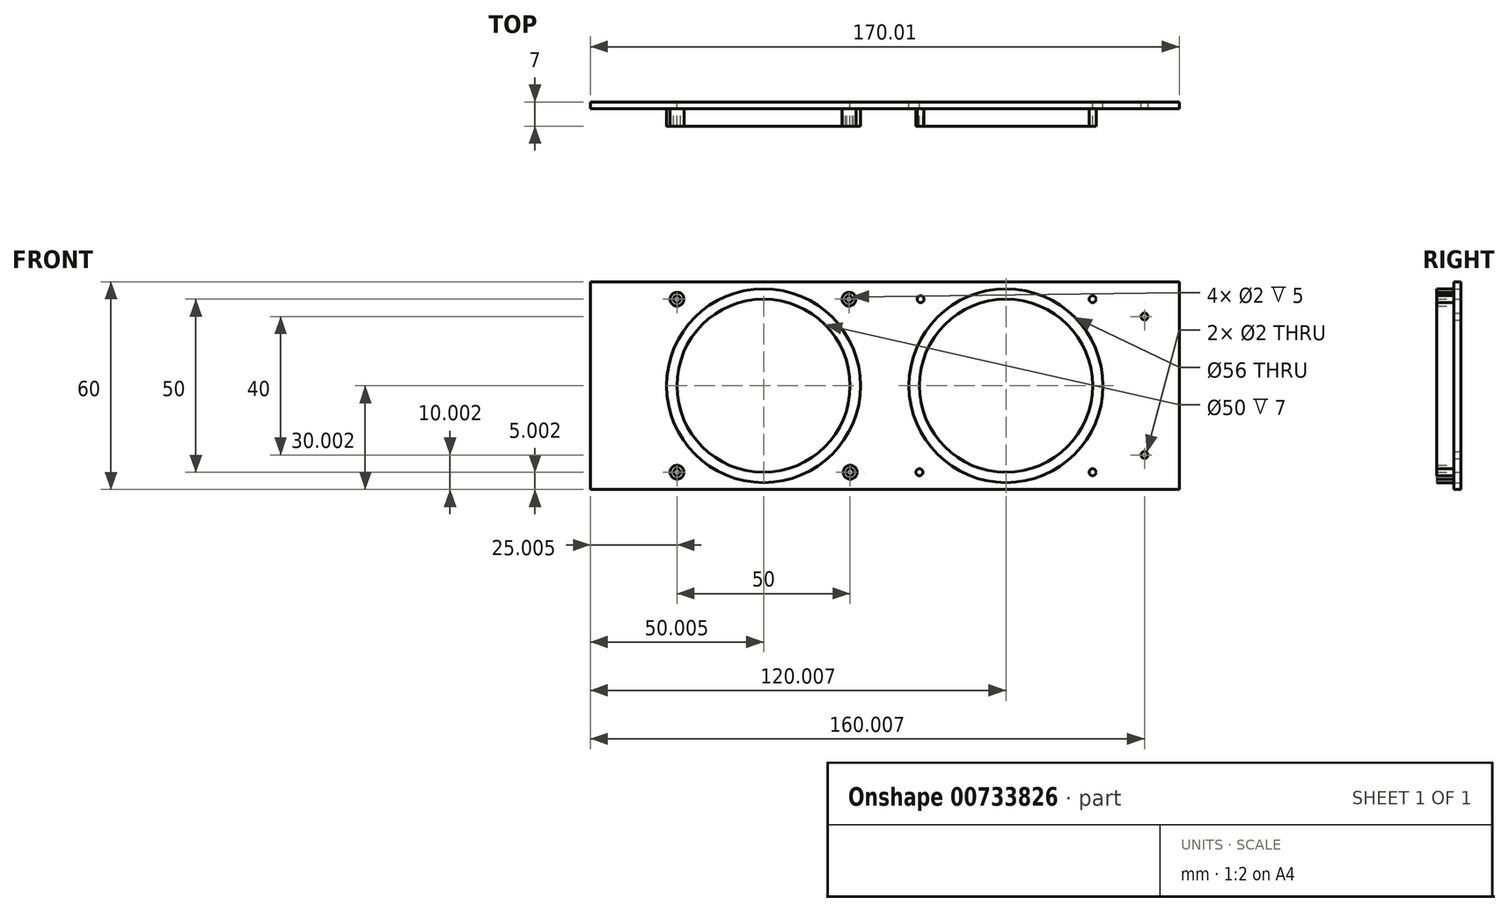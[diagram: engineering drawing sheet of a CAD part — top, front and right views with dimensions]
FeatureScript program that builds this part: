
annotation { "Feature Type Name" : "Feature", "Feature Type Description" : "" }
export const myFeature = defineFeature(function(context is Context, id is Id, definition is map)
    precondition{}
    {
        {
            var Q0;
            Q0=qCreatedBy(makeId("Front.planeOp"),FACE);
            var sketch = newSketch(context, id + "F0", { "sketchPlane" : qUnion([Q0])});
            skLineSegment(sketch, "E0.1", {"start": v(-21.17, -79.97) * mm, "end": v(-21.17, -19.97) * mm});
            skCircle(sketch, "E1", {"center": v(-11.17, -69.97) * mm, "radius": 1 * mm});
            skCircle(sketch, "E2", {"center": v(-11.17, -29.97) * mm, "radius": 1 * mm});
            skCircle(sketch, "E3", {"center": v(28.83, -49.97) * mm, "radius": 25 * mm});
            skCircle(sketch, "E4", {"center": v(53.5, -24.97) * mm, "radius": 1 * mm});
            skCircle(sketch, "E5", {"center": v(3.83, -24.97) * mm, "radius": 1 * mm});
            skCircle(sketch, "E6", {"center": v(53.83, -74.97) * mm, "radius": 1 * mm});
            skCircle(sketch, "E7", {"center": v(3.83, -74.97) * mm, "radius": 1 * mm});
            skLineSegment(sketch, "E8.MirrorCS", {"start": v(148.84, -19.97) * mm, "end": v(-21.17, -19.97) * mm});
            skLineSegment(sketch, "E9.MirrorCS", {"start": v(148.84, -79.97) * mm, "end": v(148.84, -19.97) * mm});
            skCircle(sketch, "E10.MirrorC", {"center": v(138.84, -29.97) * mm, "radius": 1 * mm});
            skCircle(sketch, "E11.MirrorC", {"center": v(138.84, -69.97) * mm, "radius": 1 * mm});
            skCircle(sketch, "E12.MirrorC", {"center": v(123.84, -74.97) * mm, "radius": 1 * mm});
            skCircle(sketch, "E13.MirrorC", {"center": v(123.84, -24.97) * mm, "radius": 1 * mm});
            skCircle(sketch, "E14.MirrorC", {"center": v(73.84, -74.97) * mm, "radius": 1 * mm});
            skCircle(sketch, "E15.MirrorC", {"center": v(74.17, -24.97) * mm, "radius": 1 * mm});
            skCircle(sketch, "E16.MirrorC", {"center": v(98.84, -49.97) * mm, "radius": 25 * mm});
            skLineSegment(sketch, "E17", {"start": v(-21.17, -79.97) * mm, "end": v(148.84, -79.97) * mm});
            skCircle(sketch, "E18", {"center": v(3.83, -24.97) * mm, "radius": 2 * mm});
            skCircle(sketch, "E19", {"center": v(3.83, -74.97) * mm, "radius": 2 * mm});
            skCircle(sketch, "E20", {"center": v(53.83, -74.97) * mm, "radius": 2 * mm});
            skCircle(sketch, "E21", {"center": v(53.5, -24.97) * mm, "radius": 2 * mm});
            skCircle(sketch, "E22", {"center": v(74.17, -24.97) * mm, "radius": 2 * mm});
            skCircle(sketch, "E23", {"center": v(73.84, -74.97) * mm, "radius": 2 * mm});
            skCircle(sketch, "E24", {"center": v(123.84, -24.97) * mm, "radius": 2 * mm});
            skCircle(sketch, "E25", {"center": v(123.84, -74.97) * mm, "radius": 2 * mm});
            skCircle(sketch, "E26", {"center": v(28.83, -49.97) * mm, "radius": 28 * mm});
            skCircle(sketch, "E27", {"center": v(98.84, -49.97) * mm, "radius": 28 * mm});
            skSolve(sketch);
        }
        {
            var Q0;
            Q0=makeQuery(id+"F0.imprint","IMPRINT",FACE,{"disambiguationData":[TD([[makeQuery(id+"F0.imprint","IMPRINT",EDGE,{"derivedFrom":sQuery(id+"F0.wireOp",EDGE,"E0.1")}),-1.0]])]});
            var Q1;
            Q1=makeQuery(id+"F0.imprint","IMPRINT",FACE,{"disambiguationData":[TD([[makeQuery(id+"F0.imprint","IMPRINT",EDGE,{"derivedFrom":sQuery(id+"F0.wireOp",EDGE,"E3")}),-1.0]])]});
            var Q2;
            Q2=makeQuery(id+"F0.imprint","IMPRINT",FACE,{"disambiguationData":[TD([[makeQuery(id+"F0.imprint","IMPRINT",EDGE,{"derivedFrom":sQuery(id+"F0.wireOp",EDGE,"E1")}),1.0]])]});
            var Q3;
            Q3=makeQuery(id+"F0.imprint","IMPRINT",FACE,{"disambiguationData":[TD([[makeQuery(id+"F0.imprint","IMPRINT",EDGE,{"derivedFrom":sQuery(id+"F0.wireOp",EDGE,"E7")}),-1.0]])]});
            var Q4;
            Q4=makeQuery(id+"F0.imprint","IMPRINT",FACE,{"disambiguationData":[TD([[makeQuery(id+"F0.imprint","IMPRINT",EDGE,{"derivedFrom":sQuery(id+"F0.wireOp",EDGE,"E7")}),1.0]])]});
            var Q5;
            Q5=makeQuery(id+"F0.imprint","IMPRINT",FACE,{"disambiguationData":[TD([[makeQuery(id+"F0.imprint","IMPRINT",EDGE,{"derivedFrom":sQuery(id+"F0.wireOp",EDGE,"E6")}),1.0]])]});
            var Q6;
            Q6=makeQuery(id+"F0.imprint","IMPRINT",FACE,{"disambiguationData":[TD([[makeQuery(id+"F0.imprint","IMPRINT",EDGE,{"derivedFrom":sQuery(id+"F0.wireOp",EDGE,"E6")}),-1.0]])]});
            var Q7;
            Q7=makeQuery(id+"F0.imprint","IMPRINT",FACE,{"disambiguationData":[TD([[makeQuery(id+"F0.imprint","IMPRINT",EDGE,{"derivedFrom":sQuery(id+"F0.wireOp",EDGE,"E14.MirrorC")}),1.0]])]});
            var Q8;
            Q8=makeQuery(id+"F0.imprint","IMPRINT",FACE,{"disambiguationData":[TD([[makeQuery(id+"F0.imprint","IMPRINT",EDGE,{"derivedFrom":sQuery(id+"F0.wireOp",EDGE,"E14.MirrorC")}),-1.0]])]});
            var Q9;
            Q9=makeQuery(id+"F0.imprint","IMPRINT",FACE,{"disambiguationData":[TD([[makeQuery(id+"F0.imprint","IMPRINT",EDGE,{"derivedFrom":sQuery(id+"F0.wireOp",EDGE,"E16.MirrorC")}),1.0]])]});
            var Q10;
            Q10=makeQuery(id+"F0.imprint","IMPRINT",FACE,{"disambiguationData":[TD([[makeQuery(id+"F0.imprint","IMPRINT",EDGE,{"derivedFrom":sQuery(id+"F0.wireOp",EDGE,"E12.MirrorC")}),1.0]])]});
            var Q11;
            Q11=makeQuery(id+"F0.imprint","IMPRINT",FACE,{"disambiguationData":[TD([[makeQuery(id+"F0.imprint","IMPRINT",EDGE,{"derivedFrom":sQuery(id+"F0.wireOp",EDGE,"E12.MirrorC")}),-1.0]])]});
            var Q12;
            Q12=makeQuery(id+"F0.imprint","IMPRINT",FACE,{"disambiguationData":[TD([[makeQuery(id+"F0.imprint","IMPRINT",EDGE,{"derivedFrom":sQuery(id+"F0.wireOp",EDGE,"E11.MirrorC")}),-1.0]])]});
            var Q13;
            Q13=makeQuery(id+"F0.imprint","IMPRINT",FACE,{"disambiguationData":[TD([[makeQuery(id+"F0.imprint","IMPRINT",EDGE,{"derivedFrom":sQuery(id+"F0.wireOp",EDGE,"E10.MirrorC")}),-1.0]])]});
            var Q14;
            Q14=makeQuery(id+"F0.imprint","IMPRINT",FACE,{"disambiguationData":[TD([[makeQuery(id+"F0.imprint","IMPRINT",EDGE,{"derivedFrom":sQuery(id+"F0.wireOp",EDGE,"E13.MirrorC")}),1.0]])]});
            var Q15;
            Q15=makeQuery(id+"F0.imprint","IMPRINT",FACE,{"disambiguationData":[TD([[makeQuery(id+"F0.imprint","IMPRINT",EDGE,{"derivedFrom":sQuery(id+"F0.wireOp",EDGE,"E13.MirrorC")}),-1.0]])]});
            var Q16;
            Q16=makeQuery(id+"F0.imprint","IMPRINT",FACE,{"disambiguationData":[TD([[makeQuery(id+"F0.imprint","IMPRINT",EDGE,{"derivedFrom":sQuery(id+"F0.wireOp",EDGE,"E15.MirrorC")}),1.0]])]});
            var Q17;
            Q17=makeQuery(id+"F0.imprint","IMPRINT",FACE,{"disambiguationData":[TD([[makeQuery(id+"F0.imprint","IMPRINT",EDGE,{"derivedFrom":sQuery(id+"F0.wireOp",EDGE,"E15.MirrorC")}),-1.0]])]});
            var Q18;
            Q18=makeQuery(id+"F0.imprint","IMPRINT",FACE,{"disambiguationData":[TD([[makeQuery(id+"F0.imprint","IMPRINT",EDGE,{"derivedFrom":sQuery(id+"F0.wireOp",EDGE,"E4")}),-1.0]])]});
            var Q19;
            Q19=makeQuery(id+"F0.imprint","IMPRINT",FACE,{"disambiguationData":[TD([[makeQuery(id+"F0.imprint","IMPRINT",EDGE,{"derivedFrom":sQuery(id+"F0.wireOp",EDGE,"E4")}),1.0]])]});
            var Q20;
            Q20=makeQuery(id+"F0.imprint","IMPRINT",FACE,{"disambiguationData":[TD([[makeQuery(id+"F0.imprint","IMPRINT",EDGE,{"derivedFrom":sQuery(id+"F0.wireOp",EDGE,"E5")}),-1.0]])]});
            var Q21;
            Q21=makeQuery(id+"F0.imprint","IMPRINT",FACE,{"disambiguationData":[TD([[makeQuery(id+"F0.imprint","IMPRINT",EDGE,{"derivedFrom":sQuery(id+"F0.wireOp",EDGE,"E5")}),1.0]])]});
            var Q22;
            Q22=makeQuery(id+"F0.imprint","IMPRINT",FACE,{"disambiguationData":[TD([[makeQuery(id+"F0.imprint","IMPRINT",EDGE,{"derivedFrom":sQuery(id+"F0.wireOp",EDGE,"E2")}),1.0]])]});
            extrude(context, id + "F1", {"entities" : qUnion([Q0, Q1, Q2, Q3, Q4, Q5, Q6, Q7, Q8, Q9, Q10, Q11, Q12, Q13, Q14, Q15, Q16, Q17, Q18, Q19, Q20, Q21, Q22]), "depth" : 5 * mm, "offsetDistance" : 25.4 * mm});
        }
        {
            var Q0;
            Q0=makeQuery(id+"F0.imprint","IMPRINT",FACE,{"disambiguationData":[TD([[makeQuery(id+"F0.imprint","IMPRINT",EDGE,{"derivedFrom":sQuery(id+"F0.wireOp",EDGE,"E5")}),-1.0]])]});
            var Q1;
            Q1=makeQuery(id+"F0.imprint","IMPRINT",FACE,{"disambiguationData":[TD([[makeQuery(id+"F0.imprint","IMPRINT",EDGE,{"derivedFrom":sQuery(id+"F0.wireOp",EDGE,"E4")}),-1.0]])]});
            var Q2;
            Q2=makeQuery(id+"F0.imprint","IMPRINT",FACE,{"disambiguationData":[TD([[makeQuery(id+"F0.imprint","IMPRINT",EDGE,{"derivedFrom":sQuery(id+"F0.wireOp",EDGE,"E15.MirrorC")}),1.0]])]});
            var Q3;
            Q3=makeQuery(id+"F0.imprint","IMPRINT",FACE,{"disambiguationData":[TD([[makeQuery(id+"F0.imprint","IMPRINT",EDGE,{"derivedFrom":sQuery(id+"F0.wireOp",EDGE,"E13.MirrorC")}),1.0]])]});
            var Q4;
            Q4=makeQuery(id+"F0.imprint","IMPRINT",FACE,{"disambiguationData":[TD([[makeQuery(id+"F0.imprint","IMPRINT",EDGE,{"derivedFrom":sQuery(id+"F0.wireOp",EDGE,"E12.MirrorC")}),1.0]])]});
            var Q5;
            Q5=makeQuery(id+"F0.imprint","IMPRINT",FACE,{"disambiguationData":[TD([[makeQuery(id+"F0.imprint","IMPRINT",EDGE,{"derivedFrom":sQuery(id+"F0.wireOp",EDGE,"E14.MirrorC")}),1.0]])]});
            var Q6;
            Q6=makeQuery(id+"F0.imprint","IMPRINT",FACE,{"disambiguationData":[TD([[makeQuery(id+"F0.imprint","IMPRINT",EDGE,{"derivedFrom":sQuery(id+"F0.wireOp",EDGE,"E6")}),-1.0]])]});
            var Q7;
            Q7=makeQuery(id+"F0.imprint","IMPRINT",FACE,{"disambiguationData":[TD([[makeQuery(id+"F0.imprint","IMPRINT",EDGE,{"derivedFrom":sQuery(id+"F0.wireOp",EDGE,"E7")}),-1.0]])]});
            extrude(context, id + "F2", {"entities" : qUnion([Q0, Q1, Q2, Q3, Q4, Q5, Q6, Q7]), "operationType" : NewBodyOperationType.ADD, "depth" : 7 * mm, "offsetDistance" : 25.4 * mm});
        }
        {
            var Q0;
            Q0=makeQuery(id+"F2.boolean.opBoolean","SPLIT",FACE,{"disambiguationData":[TD([makeQuery(id+"F2.opExtrude","SWEPT_FACE",FACE,{"disambiguationData":[OSD([sQuery(id+"F0.wireOp",EDGE,"E6")])]})])],"derivedFrom":makeQuery(id+"F1.opExtrude","CAP_FACE",FACE,{"disambiguationData":[OSD([sQuery(id+"F0.wireOp",EDGE,"E0.1"),sQuery(id+"F0.wireOp",EDGE,"E3"),sQuery(id+"F0.wireOp",EDGE,"E8.MirrorCS"),sQuery(id+"F0.wireOp",EDGE,"E9.MirrorCS"),sQuery(id+"F0.wireOp",EDGE,"E16.MirrorC"),sQuery(id+"F0.wireOp",EDGE,"E17")])],"isStart":false})});
            var Q1;
            Q1=makeQuery(id+"F2.boolean.opBoolean","SPLIT",FACE,{"disambiguationData":[TD([makeQuery(id+"F2.opExtrude","SWEPT_FACE",FACE,{"disambiguationData":[OSD([sQuery(id+"F0.wireOp",EDGE,"E14.MirrorC")])]})])],"derivedFrom":makeQuery(id+"F1.opExtrude","CAP_FACE",FACE,{"disambiguationData":[OSD([sQuery(id+"F0.wireOp",EDGE,"E0.1"),sQuery(id+"F0.wireOp",EDGE,"E3"),sQuery(id+"F0.wireOp",EDGE,"E8.MirrorCS"),sQuery(id+"F0.wireOp",EDGE,"E9.MirrorCS"),sQuery(id+"F0.wireOp",EDGE,"E16.MirrorC"),sQuery(id+"F0.wireOp",EDGE,"E17")])],"isStart":false})});
            var Q2;
            Q2=makeQuery(id+"F2.boolean.opBoolean","SPLIT",FACE,{"disambiguationData":[TD([makeQuery(id+"F2.opExtrude","SWEPT_FACE",FACE,{"disambiguationData":[OSD([sQuery(id+"F0.wireOp",EDGE,"E7")])]})])],"derivedFrom":makeQuery(id+"F1.opExtrude","CAP_FACE",FACE,{"disambiguationData":[OSD([sQuery(id+"F0.wireOp",EDGE,"E0.1"),sQuery(id+"F0.wireOp",EDGE,"E3"),sQuery(id+"F0.wireOp",EDGE,"E8.MirrorCS"),sQuery(id+"F0.wireOp",EDGE,"E9.MirrorCS"),sQuery(id+"F0.wireOp",EDGE,"E16.MirrorC"),sQuery(id+"F0.wireOp",EDGE,"E17")])],"isStart":false})});
            var Q3;
            Q3=makeQuery(id+"F2.boolean.opBoolean","SPLIT",FACE,{"disambiguationData":[TD([makeQuery(id+"F2.opExtrude","SWEPT_FACE",FACE,{"disambiguationData":[OSD([sQuery(id+"F0.wireOp",EDGE,"E5")])]})])],"derivedFrom":makeQuery(id+"F1.opExtrude","CAP_FACE",FACE,{"disambiguationData":[OSD([sQuery(id+"F0.wireOp",EDGE,"E0.1"),sQuery(id+"F0.wireOp",EDGE,"E3"),sQuery(id+"F0.wireOp",EDGE,"E8.MirrorCS"),sQuery(id+"F0.wireOp",EDGE,"E9.MirrorCS"),sQuery(id+"F0.wireOp",EDGE,"E16.MirrorC"),sQuery(id+"F0.wireOp",EDGE,"E17")])],"isStart":false})});
            var Q4;
            Q4=makeQuery(id+"F2.boolean.opBoolean","SPLIT",FACE,{"disambiguationData":[TD([makeQuery(id+"F2.opExtrude","SWEPT_FACE",FACE,{"disambiguationData":[OSD([sQuery(id+"F0.wireOp",EDGE,"E4")])]})])],"derivedFrom":makeQuery(id+"F1.opExtrude","CAP_FACE",FACE,{"disambiguationData":[OSD([sQuery(id+"F0.wireOp",EDGE,"E0.1"),sQuery(id+"F0.wireOp",EDGE,"E3"),sQuery(id+"F0.wireOp",EDGE,"E8.MirrorCS"),sQuery(id+"F0.wireOp",EDGE,"E9.MirrorCS"),sQuery(id+"F0.wireOp",EDGE,"E16.MirrorC"),sQuery(id+"F0.wireOp",EDGE,"E17")])],"isStart":false})});
            var Q5;
            Q5=makeQuery(id+"F2.boolean.opBoolean","SPLIT",FACE,{"disambiguationData":[TD([makeQuery(id+"F2.opExtrude","SWEPT_FACE",FACE,{"disambiguationData":[OSD([sQuery(id+"F0.wireOp",EDGE,"E15.MirrorC")])]})])],"derivedFrom":makeQuery(id+"F1.opExtrude","CAP_FACE",FACE,{"disambiguationData":[OSD([sQuery(id+"F0.wireOp",EDGE,"E0.1"),sQuery(id+"F0.wireOp",EDGE,"E3"),sQuery(id+"F0.wireOp",EDGE,"E8.MirrorCS"),sQuery(id+"F0.wireOp",EDGE,"E9.MirrorCS"),sQuery(id+"F0.wireOp",EDGE,"E16.MirrorC"),sQuery(id+"F0.wireOp",EDGE,"E17")])],"isStart":false})});
            var Q6;
            Q6=makeQuery(id+"F2.boolean.opBoolean","SPLIT",FACE,{"disambiguationData":[TD([makeQuery(id+"F2.opExtrude","SWEPT_FACE",FACE,{"disambiguationData":[OSD([sQuery(id+"F0.wireOp",EDGE,"E13.MirrorC")])]})])],"derivedFrom":makeQuery(id+"F1.opExtrude","CAP_FACE",FACE,{"disambiguationData":[OSD([sQuery(id+"F0.wireOp",EDGE,"E0.1"),sQuery(id+"F0.wireOp",EDGE,"E3"),sQuery(id+"F0.wireOp",EDGE,"E8.MirrorCS"),sQuery(id+"F0.wireOp",EDGE,"E9.MirrorCS"),sQuery(id+"F0.wireOp",EDGE,"E16.MirrorC"),sQuery(id+"F0.wireOp",EDGE,"E17")])],"isStart":false})});
            var Q7;
            Q7=makeQuery(id+"F2.boolean.opBoolean","SPLIT",FACE,{"disambiguationData":[TD([makeQuery(id+"F2.opExtrude","SWEPT_FACE",FACE,{"disambiguationData":[OSD([sQuery(id+"F0.wireOp",EDGE,"E12.MirrorC")])]})])],"derivedFrom":makeQuery(id+"F1.opExtrude","CAP_FACE",FACE,{"disambiguationData":[OSD([sQuery(id+"F0.wireOp",EDGE,"E0.1"),sQuery(id+"F0.wireOp",EDGE,"E3"),sQuery(id+"F0.wireOp",EDGE,"E8.MirrorCS"),sQuery(id+"F0.wireOp",EDGE,"E9.MirrorCS"),sQuery(id+"F0.wireOp",EDGE,"E16.MirrorC"),sQuery(id+"F0.wireOp",EDGE,"E17")])],"isStart":false})});
            extrude(context, id + "F3", {"entities" : qUnion([Q0, Q1, Q2, Q3, Q4, Q5, Q6, Q7]), "operationType" : NewBodyOperationType.REMOVE, "oppositeDirection" : true, "depth" : 3 * mm, "offsetDistance" : 25.4 * mm});
        }
        {
            var Q0;
            Q0=makeQuery(id+"F0.imprint","IMPRINT",FACE,{"disambiguationData":[TD([[makeQuery(id+"F0.imprint","IMPRINT",EDGE,{"derivedFrom":sQuery(id+"F0.wireOp",EDGE,"E16.MirrorC")}),1.0]])]});
            var Q1;
            Q1=makeQuery(id+"F0.imprint","IMPRINT",FACE,{"disambiguationData":[TD([[makeQuery(id+"F0.imprint","IMPRINT",EDGE,{"derivedFrom":sQuery(id+"F0.wireOp",EDGE,"E3")}),-1.0]])]});
            extrude(context, id + "F4", {"entities" : qUnion([Q0, Q1]), "operationType" : NewBodyOperationType.ADD, "depth" : 7 * mm, "offsetDistance" : 25.4 * mm});
        }
        {
            var Q0;
            Q0=makeQuery(id+"F0.imprint","IMPRINT",FACE,{"disambiguationData":[TD([[makeQuery(id+"F0.imprint","IMPRINT",EDGE,{"derivedFrom":sQuery(id+"F0.wireOp",EDGE,"E2")}),1.0]])]});
            var Q1;
            Q1=makeQuery(id+"F0.imprint","IMPRINT",FACE,{"disambiguationData":[TD([[makeQuery(id+"F0.imprint","IMPRINT",EDGE,{"derivedFrom":sQuery(id+"F0.wireOp",EDGE,"E10.MirrorC")}),-1.0]])]});
            var Q2;
            Q2=makeQuery(id+"F0.imprint","IMPRINT",FACE,{"disambiguationData":[TD([[makeQuery(id+"F0.imprint","IMPRINT",EDGE,{"derivedFrom":sQuery(id+"F0.wireOp",EDGE,"E11.MirrorC")}),-1.0]])]});
            var Q3;
            Q3=makeQuery(id+"F0.imprint","IMPRINT",FACE,{"disambiguationData":[TD([[makeQuery(id+"F0.imprint","IMPRINT",EDGE,{"derivedFrom":sQuery(id+"F0.wireOp",EDGE,"E1")}),1.0]])]});
            extrude(context, id + "F5", {"entities" : qUnion([Q0, Q1, Q2, Q3]), "operationType" : NewBodyOperationType.REMOVE, "depth" : 5 * mm, "offsetDistance" : 25.4 * mm, "hasSecondDirection" : true, "secondDirectionOppositeDirection" : false, "secondDirectionDepth" : 2 * mm});
        }
    });
